FCSTD DOCUMENT  (FreeCAD 2021.0226R23964 +3297 (Git))
Label: loft
License: All rights reserved
LicenseURL: http://en.wikipedia.org/wiki/All_rights_reserved
objects: Sketcher::SketchObject×3, PartDesign::Plane×1, PartDesign::Body×1, App::Part×1
note: 5 computed .brp shape members not serialized (recipe doc carries the construction recipe); baked Part::Feature solids carry a one-line shape summary decoded from their .brp

FEATURE [Sketcher::SketchObject] Sketch
  AttachmentOffset = pos=(0,0,-35) rot=(0,0,1;0rad)
  FullyConstrained = true
  MapMode = 5
  Placement = pos=(-35,7.8e-15,-7.8e-15) rot=(0.57735,0.57735,0.57735;2.0944rad)
  Support = -> [YZ_Plane]
  sketch-geometry (12):
    g0: ArcOfCircle CenterX=-40 CenterY=15 CenterZ=0 NormalX=0 NormalY=0 NormalZ=1 AngleXU=0 Radius=3 StartAngle=1.5708 EndAngle=3.14159
    g1: ArcOfCircle CenterX=40 CenterY=15 CenterZ=0 NormalX=0 NormalY=0 NormalZ=1 AngleXU=0 Radius=3 StartAngle=0 EndAngle=1.5708
    g2: ArcOfCircle CenterX=-42 CenterY=-15 CenterZ=0 NormalX=0 NormalY=0 NormalZ=1 AngleXU=0 Radius=1 StartAngle=3.14159 EndAngle=4.71239
    g3: ArcOfCircle CenterX=42 CenterY=-15 CenterZ=0 NormalX=0 NormalY=0 NormalZ=1 AngleXU=0 Radius=1 StartAngle=4.71239 EndAngle=6.28319
    g4: LineSegment StartX=-40 StartY=18 StartZ=0 EndX=40 EndY=18 EndZ=0
    g5: LineSegment StartX=-43 StartY=15 StartZ=0 EndX=-43 EndY=-15 EndZ=0
    g6: LineSegment StartX=43 StartY=15 StartZ=0 EndX=43 EndY=-15 EndZ=0
    g7: ArcOfCircle CenterX=-42 CenterY=-18 CenterZ=0 NormalX=0 NormalY=0 NormalZ=1 AngleXU=0 Radius=2 StartAngle=-9e-16 EndAngle=1.5708
    g8: ArcOfCircle CenterX=42 CenterY=-18 CenterZ=0 NormalX=0 NormalY=0 NormalZ=1 AngleXU=0 Radius=2 StartAngle=1.5708 EndAngle=3.14159
    g9: LineSegment StartX=-40 StartY=-18 StartZ=0 EndX=-40 EndY=-30 EndZ=0
    g10: LineSegment StartX=-40 StartY=-30 StartZ=0 EndX=40 EndY=-30 EndZ=0
    g11: LineSegment StartX=40 StartY=-30 StartZ=0 EndX=40 EndY=-18 EndZ=0
  constraints (32):
    c: Horizontal(g4)
    c: Vertical(g6)
    c: Vertical(g9)
    c: Coincident(g9,g10)
    c: Horizontal(g10)
    c: Coincident(g10,g11)
    c: Vertical(g11)
    c: Equal(g5,g6)
    c: Equal(g0,g1)
    c: Vertical(g5)
    c: Radius(g0) = 3
    c: Radius(g2) = 1
    c: DistanceX(g4,g4) = 80
    c: Equal(g2,g3)
    c: Equal(g7,g8)
    c: Tangent(g4,g1) = 1.5708
    c: Tangent(g6,g1) = 1.5708
    c: Tangent(g4,g0) = 1.5708
    c: Tangent(g5,g0) = -1.5708
    c: DistanceY(g5,g5) = 30
    c: DistanceY(g0,g-1) = -15
    c: Tangent(g5,g2) = -1.5708
    c: Tangent(g7,g2) = 1.5708
    c: Tangent(g9,g7) = 1.5708
    c: Tangent(g11,g8) = 1.5708
    c: Tangent(g6,g3) = 1.5708
    c: Tangent(g8,g3) = 1.5708
    c: DistanceY(g9,g-1) = 30
    c: Radius(g8) = 2
    c: Vertical(g8,g3)
    c: Vertical(g2,g7)
    c: DistanceX(g0,g-1) = 40
FEATURE [Sketcher::SketchObject] Sketch001
  AttachmentOffset = pos=(0,0,35) rot=(0,0,1;0rad)
  FullyConstrained = true
  MapMode = 5
  Placement = pos=(35,-7.8e-15,7.8e-15) rot=(0.57735,0.57735,0.57735;2.0944rad)
  Support = -> [YZ_Plane]
  sketch-geometry (6):
    g0: ArcOfCircle CenterX=-44 CenterY=21 CenterZ=0 NormalX=0 NormalY=0 NormalZ=1 AngleXU=0 Radius=5 StartAngle=1.5708 EndAngle=3.14159
    g1: LineSegment StartX=-44 StartY=26 StartZ=0 EndX=44 EndY=26 EndZ=0
    g2: ArcOfCircle CenterX=44 CenterY=21 CenterZ=0 NormalX=0 NormalY=0 NormalZ=1 AngleXU=0 Radius=5 StartAngle=3.6e-15 EndAngle=1.5708
    g3: LineSegment StartX=-49 StartY=21 StartZ=0 EndX=-49 EndY=-30 EndZ=0
    g4: LineSegment StartX=-49 StartY=-30 StartZ=0 EndX=49 EndY=-30 EndZ=0
    g5: LineSegment StartX=49 StartY=21 StartZ=0 EndX=49 EndY=-30 EndZ=0
  constraints (17):
    c: Horizontal(g1)
    c: Coincident(g3,g0)
    c: Vertical(g3)
    c: Coincident(g4,g3)
    c: Horizontal(g4)
    c: Coincident(g5,g4)
    c: Vertical(g5)
    c: Equal(g0,g2)
    c: DistanceY(g3,g-1) = 30
    c: DistanceX(g0,g-1) = 44
    c: Tangent(g1,g0) = 1.5708
    c: Radius(g0) = 5
    c: Horizontal(g0,g0)
    c: DistanceX(g-1,g1) = 44
    c: DistanceY(g-1,g0) = 26
    c: Tangent(g1,g2) = 1.5708
    c: Tangent(g2,g5) = 1.5708
FEATURE [PartDesign::Plane] DatumPlane
  Length = 81.9256
  MapMode = 13
  MinimumLength = 10
  MinimumWidth = 10
  Placement = pos=(11.6667,-46,-9) rot=(0.045224,0.706383,0.706383;3.05121rad)
  ResizeMode = 0
  Support = -> [Sketch001,Sketch]
  Width = 56
FEATURE [Sketcher::SketchObject] Sketch002
  ExternalGeometry = -> [Sketch,Sketch001]
  FullyConstrained = false
  MapMode = 5
  Placement = pos=(11.6667,-46,-9) rot=(0.045224,0.706383,0.706383;3.05121rad)
  Support = -> [DatumPlane]
  sketch-geometry (2):
    g0: LineSegment StartX=47.0508 StartY=-21 StartZ=0 EndX=-23.5254 EndY=-21 EndZ=0
    g1: ArcOfCircle CenterX=20.1194 CenterY=225.096 CenterZ=0 NormalX=0 NormalY=0 NormalZ=1 AngleXU=0 Radius=199.918 StartAngle=4.4923 EndAngle=4.84751
  constraints (4):
    c: Coincident(g0,g-3)
    c: Coincident(g0,g-4)
    c: Coincident(g1,g-5)
    c: Coincident(g1,g-6)
FEATURE [PartDesign::Body] Body
  AutoGroupSolids = false
  ExportMode = 0
  Group = -> [Sketch,Sketch001,DatumPlane,Sketch002]
  Origin = -> Origin001
  _ExportChildren = -> [Sketch,Sketch001,DatumPlane,Sketch002]
  _GroupVersion = 1
FEATURE [App::Part] Part
  ExportMode = 1
  Group = -> [Body]
  Origin = -> Origin
  _ExportChildren = -> [Body]
  _GroupVersion = 1
